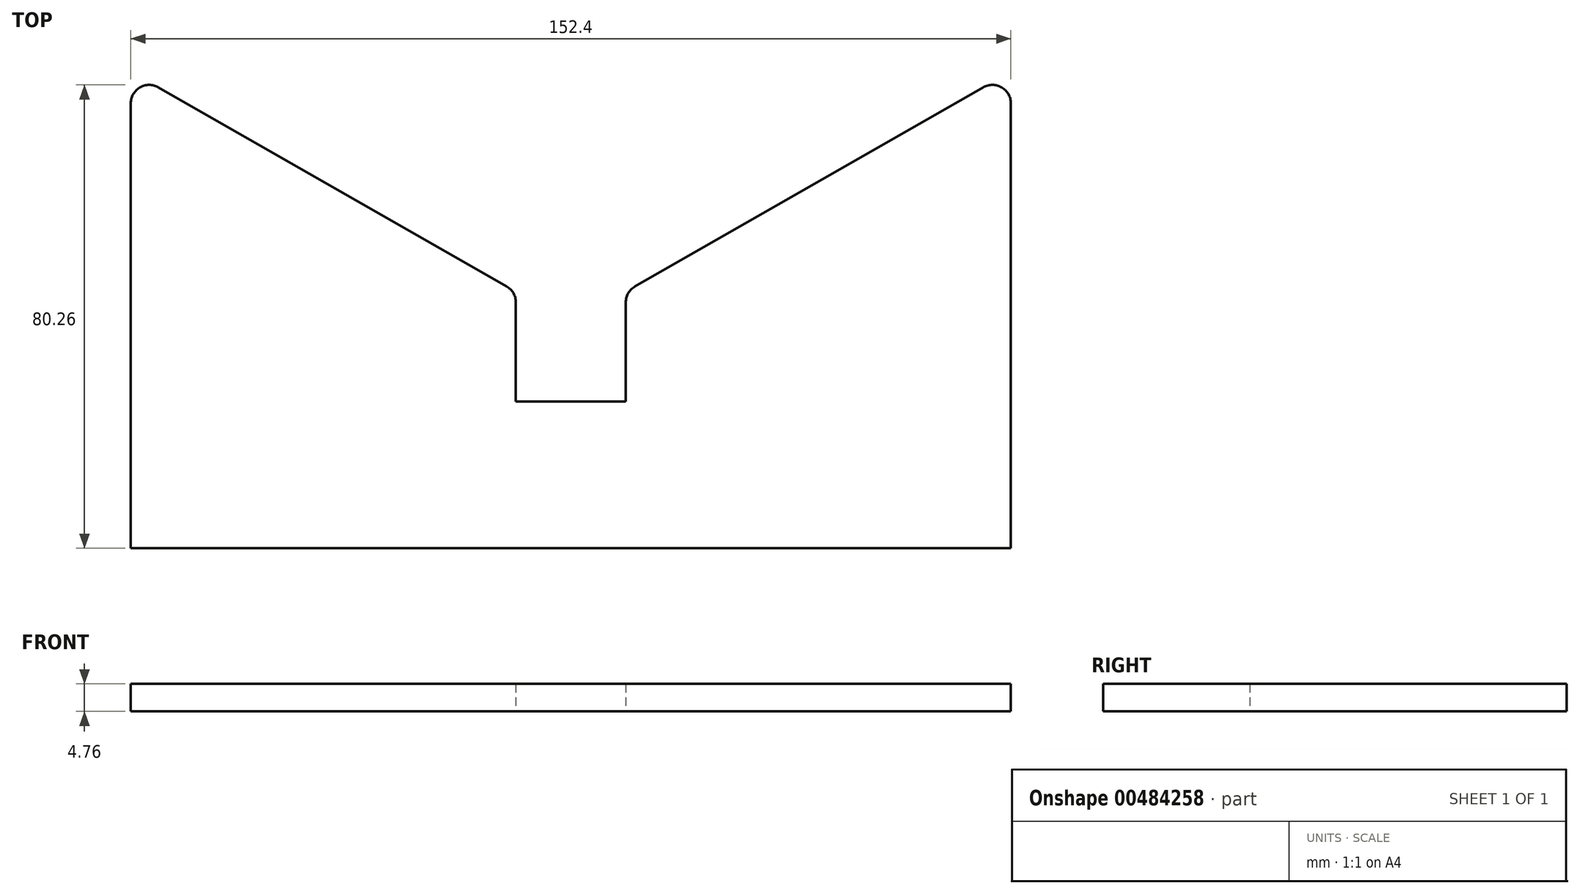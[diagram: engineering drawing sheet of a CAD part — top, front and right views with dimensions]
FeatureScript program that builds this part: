
annotation { "Feature Type Name" : "Feature", "Feature Type Description" : "" }
export const myFeature = defineFeature(function(context is Context, id is Id, definition is map)
    precondition{}
    {
        {
            var Q0;
            Q0=qCreatedBy(makeId("Top.planeOp"),FACE);
            var sketch = newSketch(context, id + "F0", { "sketchPlane" : qUnion([Q0])});
            skLineSegment(sketch, "E0.top", {"start": v(76.2, -41.28) * mm, "end": v(-76.2, -41.28) * mm});
            skLineSegment(sketch, "E0.left", {"start": v(76.2, 35.8) * mm, "end": v(76.2, -41.28) * mm});
            skLineSegment(sketch, "E0.right", {"start": v(-76.2, 35.8) * mm, "end": v(-76.2, -41.28) * mm});
            skPoint(sketch, "E0.middle", {"position": v(0, 0) * mm});
            skLineSegment(sketch, "E1.bottom", {"start": v(9.52, -15.88) * mm, "end": v(-9.53, -15.88) * mm});
            skLineSegment(sketch, "E1.left", {"start": v(9.52, -15.88) * mm, "end": v(9.53, 1.33) * mm});
            skLineSegment(sketch, "E1.right", {"start": v(-9.53, -15.88) * mm, "end": v(-9.53, 1.33) * mm});
            skPoint(sketch, "E2", {"position": v(-9.53, 3.17) * mm});
            skPoint(sketch, "E3", {"position": v(9.53, 3.17) * mm});
            skLineSegment(sketch, "E4", {"start": v(-11.12, 4.09) * mm, "end": v(-71.45, 38.56) * mm});
            skLineSegment(sketch, "E5", {"start": v(11.12, 4.09) * mm, "end": v(71.45, 38.56) * mm});
            skPoint(sketch, "E6.orphan", {"position": v(-9.52, 15.88) * mm});
            skPoint(sketch, "E7.orphan", {"position": v(9.53, 15.88) * mm});
            skPoint(sketch, "E8.visualSharp", {"position": v(-76.2, 41.28) * mm});
            skArc(sketch, "E8.filletArc", {"start": v(-71.45, 38.56) * mm, "mid": v(-74.62, 38.55) * mm, "end": v(-76.2, 35.8) * mm});
            skPoint(sketch, "E9.visualSharp", {"position": v(76.2, 41.28) * mm});
            skArc(sketch, "E9.filletArc", {"start": v(76.2, 35.8) * mm, "mid": v(74.62, 38.55) * mm, "end": v(71.45, 38.56) * mm});
            skPoint(sketch, "E10.visualSharp", {"position": v(9.52, 3.17) * mm});
            skArc(sketch, "E10.filletArc", {"start": v(11.12, 4.09) * mm, "mid": v(9.95, 2.93) * mm, "end": v(9.53, 1.33) * mm});
            skArc(sketch, "E11.filletArc", {"start": v(-9.53, 1.33) * mm, "mid": v(-9.95, 2.93) * mm, "end": v(-11.12, 4.09) * mm});
            skSolve(sketch);
        }
        {
            var Q0;
            Q0=makeQuery(id+"F0.imprint","IMPRINT",FACE,{"disambiguationData":[TD([[makeQuery(id+"F0.imprint","IMPRINT",EDGE,{"derivedFrom":sQuery(id+"F0.wireOp",EDGE,"E0.top")}),-1.0]])]});
            extrude(context, id + "F1", {"entities" : qUnion([Q0]), "depth" : 4.76 * mm});
        }
    });
